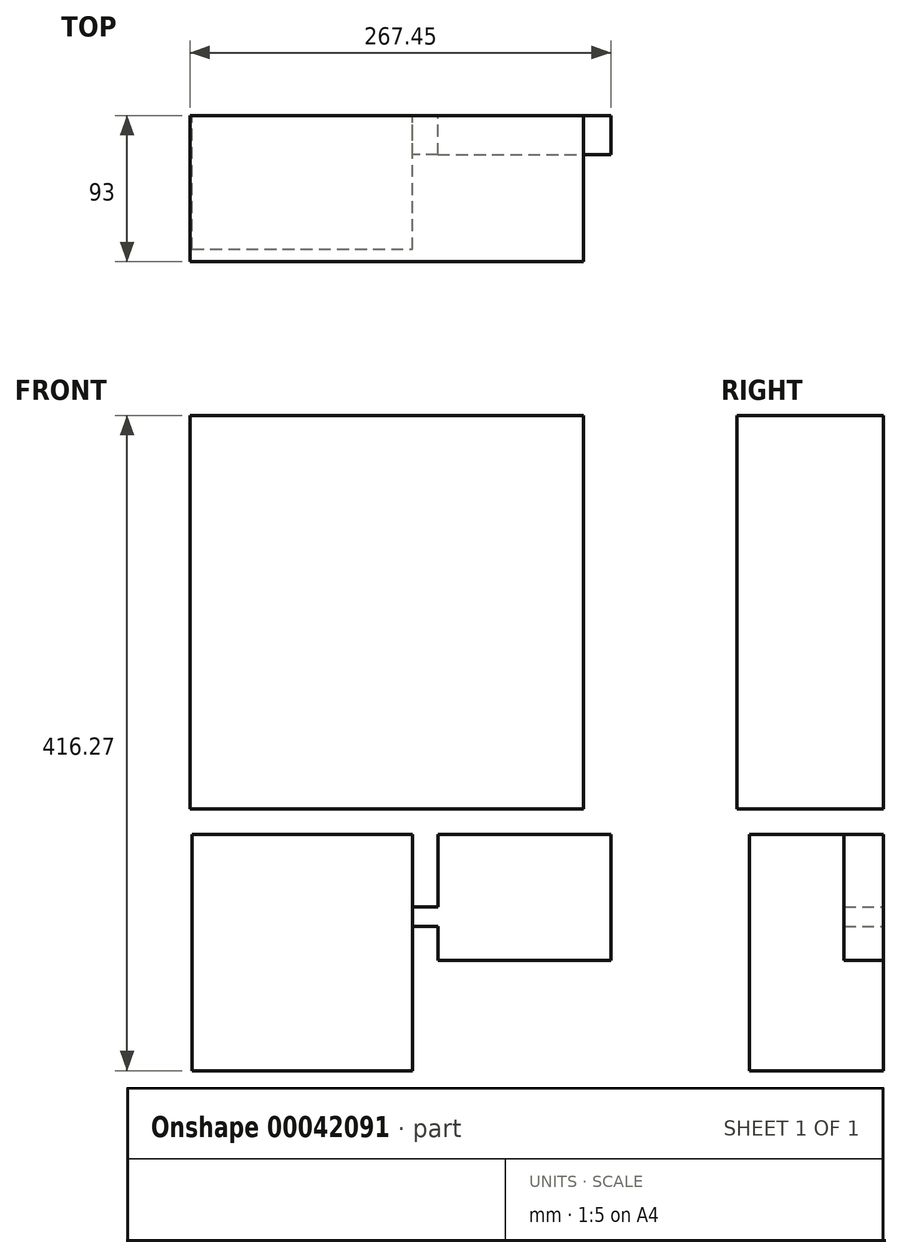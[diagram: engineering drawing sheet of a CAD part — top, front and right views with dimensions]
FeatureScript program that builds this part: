
annotation { "Feature Type Name" : "Feature", "Feature Type Description" : "" }
export const myFeature = defineFeature(function(context is Context, id is Id, definition is map)
    precondition{}
    {
        {
            var Q0;
            Q0=qCreatedBy(makeId("Front.planeOp"),FACE);
            var sketch = newSketch(context, id + "F0", { "sketchPlane" : qUnion([Q0])});
            skLineSegment(sketch, "E0.rect.bottom", {"start": v(-125, 125) * mm, "end": v(125, 125) * mm});
            skLineSegment(sketch, "E0.rect.top", {"start": v(-125, -125) * mm, "end": v(125, -125) * mm});
            skLineSegment(sketch, "E0.rect.left", {"start": v(-125, 125) * mm, "end": v(-125, -125) * mm});
            skLineSegment(sketch, "E0.rect.right", {"start": v(125, 125) * mm, "end": v(125, -125) * mm});
            skPoint(sketch, "E0.rect.middle", {"position": v(0, 0) * mm});
            skLineSegment(sketch, "E1.bottom", {"start": v(-123.63, -141.27) * mm, "end": v(16.37, -141.27) * mm});
            skLineSegment(sketch, "E1.top", {"start": v(-123.63, -291.27) * mm, "end": v(16.37, -291.27) * mm});
            skLineSegment(sketch, "E1.left", {"start": v(-123.63, -141.27) * mm, "end": v(-123.63, -291.27) * mm});
            skLineSegment(sketch, "E1.right", {"start": v(16.37, -141.27) * mm, "end": v(16.37, -291.27) * mm});
            skLineSegment(sketch, "E2.bottom", {"start": v(-75.08, -125) * mm, "end": v(-61.2, -125) * mm});
            skLineSegment(sketch, "E2.top", {"start": v(-75.08, -141.27) * mm, "end": v(-61.2, -141.27) * mm});
            skLineSegment(sketch, "E2.left", {"start": v(-75.08, -125) * mm, "end": v(-75.08, -141.27) * mm});
            skLineSegment(sketch, "E2.right", {"start": v(-61.2, -125) * mm, "end": v(-61.2, -141.27) * mm});
            skLineSegment(sketch, "E3.bottom", {"start": v(32.45, -187.24) * mm, "end": v(16.37, -187.24) * mm});
            skLineSegment(sketch, "E3.top", {"start": v(32.45, -199.5) * mm, "end": v(16.37, -199.5) * mm});
            skLineSegment(sketch, "E3.left", {"start": v(32.45, -187.24) * mm, "end": v(32.45, -199.5) * mm});
            skLineSegment(sketch, "E3.right", {"start": v(16.37, -187.24) * mm, "end": v(16.37, -199.5) * mm});
            skLineSegment(sketch, "E4.bottom", {"start": v(32.45, -141.27) * mm, "end": v(142.45, -141.27) * mm});
            skLineSegment(sketch, "E4.top", {"start": v(32.45, -221.27) * mm, "end": v(142.45, -221.27) * mm});
            skLineSegment(sketch, "E4.left", {"start": v(32.45, -141.27) * mm, "end": v(32.45, -221.27) * mm});
            skLineSegment(sketch, "E4.right", {"start": v(142.45, -141.27) * mm, "end": v(142.45, -221.27) * mm});
            skSolve(sketch);
        }
        {
            var Q0;
            Q0=makeQuery(id+"F0.imprint","IMPRINT",FACE,{"disambiguationData":[TD([[makeQuery(id+"F0.imprint","IMPRINT",EDGE,{"derivedFrom":sQuery(id+"F0.wireOp",EDGE,"E1.bottom")}),-1.0]])]});
            extrude(context, id + "F1", {"entities" : qUnion([Q0]), "depth" : 85 * mm});
        }
        {
            var Q0;
            Q0=makeQuery(id+"F0.imprint","IMPRINT",FACE,{"disambiguationData":[TD([[makeQuery(id+"F0.imprint","IMPRINT",EDGE,{"derivedFrom":sQuery(id+"F0.wireOp",EDGE,"E2.bottom")}),-1.0]])]});
            var Q1;
            Q1=makeQuery(id+"F0.imprint","IMPRINT",FACE,{"disambiguationData":[TD([[makeQuery(id+"F0.imprint","IMPRINT",EDGE,{"derivedFrom":sQuery(id+"F0.wireOp",EDGE,"E3.bottom")}),1.0]])]});
            extrude(context, id + "F2", {"entities" : qUnion([Q0, Q1]), "operationType" : NewBodyOperationType.ADD, "depth" : 25 * mm});
        }
        {
            var Q0;
            Q0=makeQuery(id+"F0.imprint","IMPRINT",FACE,{"disambiguationData":[TD([[makeQuery(id+"F0.imprint","IMPRINT",EDGE,{"derivedFrom":sQuery(id+"F0.wireOp",EDGE,"E0.rect.bottom")}),-1.0]])]});
            extrude(context, id + "F3", {"entities" : qUnion([Q0]), "operationType" : NewBodyOperationType.ADD, "depth" : 93 * mm});
        }
        {
            var Q0;
            {var subQ3=sQuery(id+"F0.wireOp",EDGE,"E4.bottom");Q0=makeQuery(id+"F0.imprint","IMPRINT",FACE,{"disambiguationData":[TD([[makeQuery(id+"F0.imprint","IMPRINT",EDGE,{"derivedFrom":subQ3}),-1.0]])]});}
            extrude(context, id + "F4", {"entities" : qUnion([Q0]), "operationType" : NewBodyOperationType.ADD, "depth" : 25 * mm});
        }
    });
